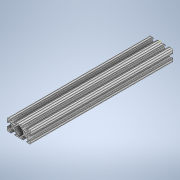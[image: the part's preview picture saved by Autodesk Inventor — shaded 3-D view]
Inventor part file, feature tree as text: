
AUTODESK INVENTOR PART (.ipt)
format: ipt  version: 2020 (Build 240168000, 168)  size: 332,800 bytes
history: native  units: in
note: dims shown in document units (in); Inventor stores cm internally (conversion verified against a paired STEP export)
features: sketch x2, extrude x1
ambient origin geometry x8: Origin, YZ Plane, XZ Plane, XY Plane, X Axis, Y Axis, Z Axis, Center Point
bodies: Solid1 (feature_tree)
feature tree (3):
  extrude  "Extrusion1"  [1 undecoded]
  sketch  "Sketch2"
  sketch  "Sketch1"  dims[d0=12.0in d1=0.0in]
note: 1 required parameter value undecoded (feature->parameter linkage not recoverable at this tier; creation-order binding heuristic only, values carry confidence <= 0.55)
